# Revit family: Shower-Valve_Trim-KOHLER-Vive-K-23971IN
name_source: partatom
category: Specialty Equipment
units: mm (PartAtom-declared; Revit-internal decimal feet)

## family parameters
Cut with Voids When Loaded = No
Host = Face
Maintain Annotation Orientation = No
OmniClass Number = 23.31.25.00
Part Type = Normal
Room Calculation Point = No
Round Connector Dimension = Use Diameter
Shared = No

## types (6) — shared parameters
ADA Compliant = No
Assembly Code = C1030200
Date Modified = 07/24/2024
Default Elevation = 1066.8 mm
Description = Aqua Turbo 235 Rbs Trim
Handle Clearance = 89 mm  [stored 0.291995 ft]
Height = 187.027 mm
Manufacturer = Kohler Co.
Master Format 2014 = 10 28 00
Master Format 2014 Name = Toilet, Bath, and Laundry Accessories
Material = Premium Metal Construction
Product Name = Vive
URL = https://www.kohler.co.in
WaterSense Certified = No
Width = 140.99 mm

## per-type parameters (varying)
| type | Finish | Length | Model | Product Page URL | Type |
| 4FP, CP-Polished Chrome | Kohler-Metal-CP-Polished_Chrome | 106 mm  [stored 0.347769 ft] | K- 23971IN-4FP-CP | https://www.kohler.co.in | 2 |
| 4FP, AF-Vibrant French Gold | Kohler-Metal-AF-Vibrant_French_Gold | 106 mm  [stored 0.347769 ft] | K- 23971IN-4FP-AF | https://www.kohler.co.in | 1 |
| 4FP, RGD-Polished Rose Gold | Kohler-Metal-RGD-Polished_Rose_Gold | 106 mm  [stored 0.347769 ft] | K- 23971IN-4FP-RGD | https://www.kohler.co.in | 3 |
| 4FS, AF-Vibrant French Gold | Kohler-Metal-AF-Vibrant_French_Gold | 117.1 mm  [stored 0.384186 ft] | K- 23971IN-4FS-AF |  | 4 |
| 4FS, CP-Polished Chrome | Kohler-Metal-CP-Polished_Chrome | 117.1 mm  [stored 0.384186 ft] | K- 23971IN-4FS-CP |  | 5 |
| 4FS, RGD-Polished Rose Gold | Kohler-Metal-RGD-Polished_Rose_Gold | 117.1 mm  [stored 0.384186 ft] | K- 23971IN-4FS-RGD |  | 6 |

note: [stored X ft] marks values corroborated as IEEE doubles in the binary element streams (Revit-internal decimal feet)

## geometry (parser evidence)
native form markers: Sweep x8
no freeform markers — native parametric forms only
